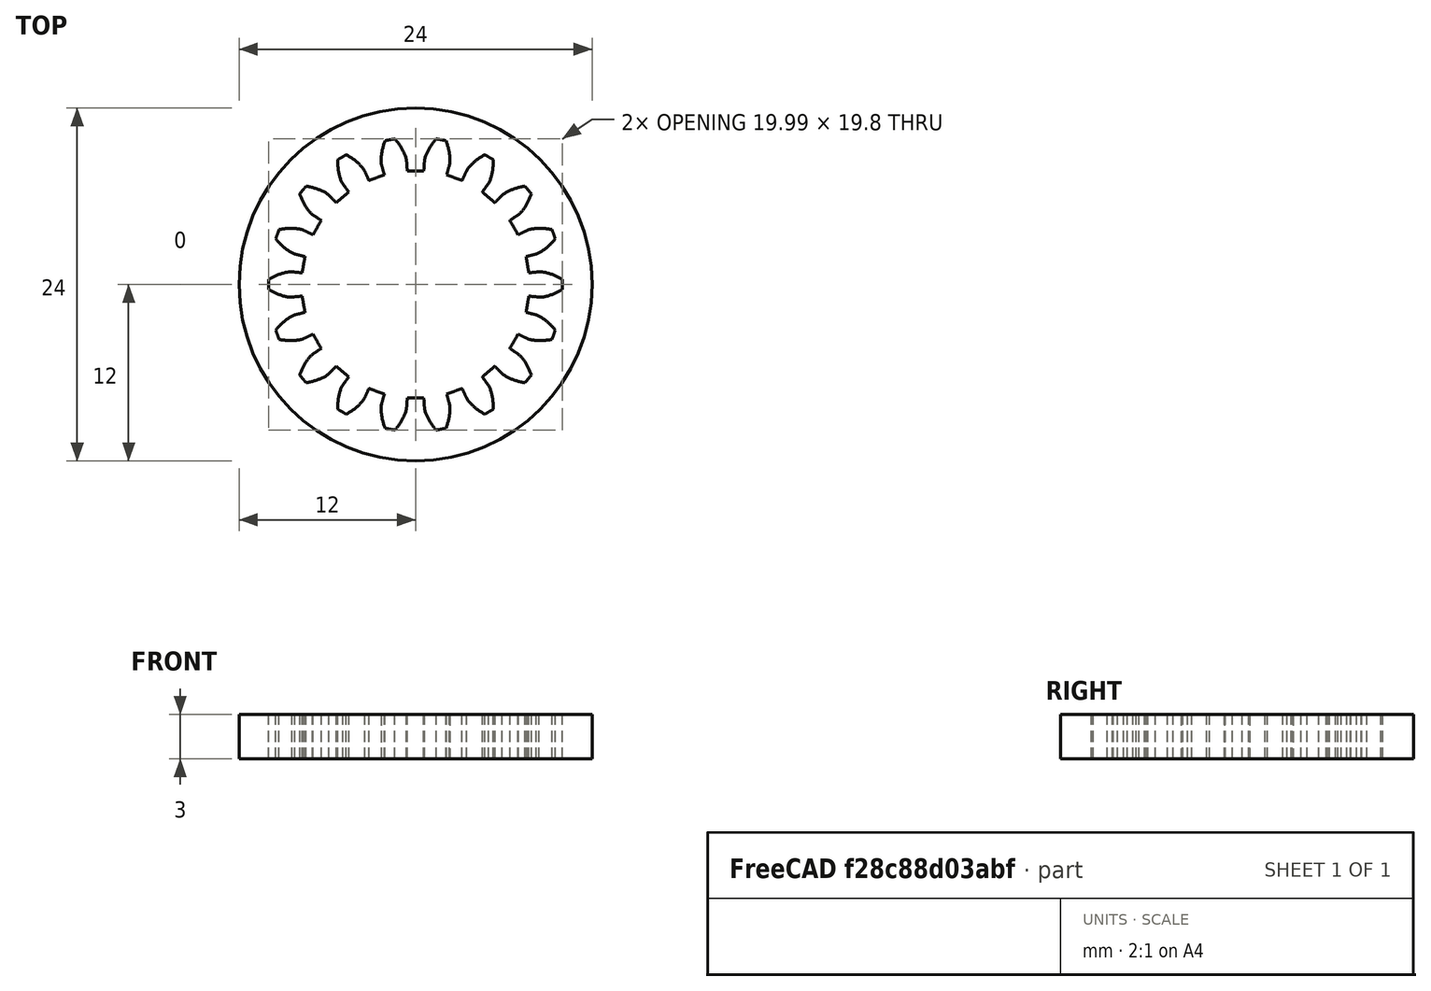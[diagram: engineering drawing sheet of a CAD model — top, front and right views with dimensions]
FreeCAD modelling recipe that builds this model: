
FCSTD DOCUMENT  (FreeCAD 0.19R24276 (Git))
Label: Gear_privod_perehodnik_to_GT2_test_3mm_zazor_05
License: All rights reserved
LicenseURL: http://en.wikipedia.org/wiki/All_rights_reserved
objects: Sketcher::SketchObject×1, PartDesign::FeaturePython×1, PartDesign::Pad×1, PartDesign::Body×1, Part::Cut×1
note: 6 computed .brp shape members not serialized (recipe doc carries the construction recipe); baked Part::Feature solids carry a one-line shape summary decoded from their .brp

FEATURE [Sketcher::SketchObject] Sketch
  FullyConstrained = true
  MapMode = 5
  Support = -> [XY_Plane]
  sketch-geometry (1):
    g0: Circle CenterX=0 CenterY=0 CenterZ=0 NormalX=0 NormalY=0 NormalZ=1 AngleXU=0 Radius=12
  constraints (2):
    c: Coincident(g0,g-1)
    c: Diameter(g0) = 24
FEATURE [PartDesign::FeaturePython] involutegear  # WARN: FeaturePython — macro-defined, semantics opaque (R4)
  AttacherType = Attacher::AttachEngine3D
  backlash = 0
  beta = 0
  clearance = 0.25
  da = 20
  df = 15.5
  double_helix = false
  dw = 18
  head = 0
  height = 3
  module = 1
  numpoints = 6
  pressure_angle = 20
  properties_from_tool = false
  reversed_backlash = false
  shift = 0
  simple = false
  teeth = 18
  transverse_pitch = 3.14159
  undercut = false
  version = 0.0.3
FEATURE [PartDesign::Pad] Pad
  BaseFeature = -> involutegear
  Direction = (1,1,1)
  Length = 3
  Length2 = 100
  Profile = -> Sketch
  Type = 0
FEATURE [PartDesign::Body] Body
  Group = -> [Sketch,involutegear,Pad]
  Origin = -> Origin
  Tip = -> Pad
FEATURE [Part::Cut] Cut
  Base = -> Pad
  Tool = -> involutegear
